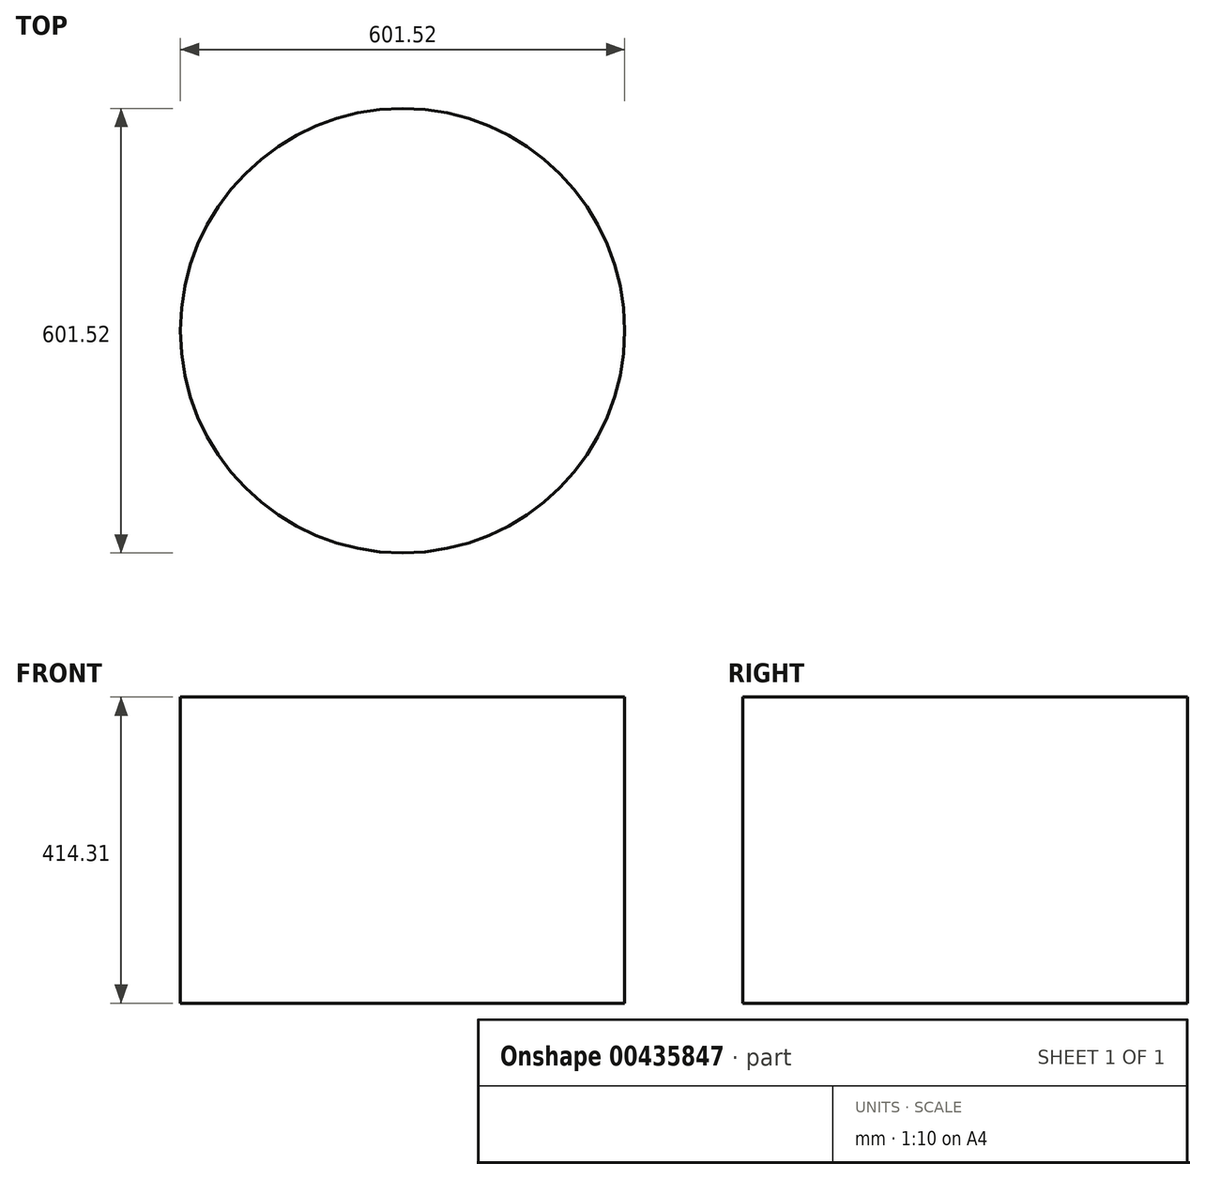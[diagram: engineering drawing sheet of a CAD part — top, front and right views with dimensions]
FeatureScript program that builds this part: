
annotation { "Feature Type Name" : "Feature", "Feature Type Description" : "" }
export const myFeature = defineFeature(function(context is Context, id is Id, definition is map)
    precondition{}
    {
        {
            var Q0;
            Q0=qCreatedBy(makeId("Top.planeOp"),FACE);
            var sketch = newSketch(context, id + "F0", { "sketchPlane" : qUnion([Q0])});
            skCircle(sketch, "E0", {"center": v(-114.9, 244.31) * mm, "radius": 300.76 * mm});
            skSolve(sketch);
        }
        {
            var Q0;
            Q0 = qSketchRegion(id + "F0", true);
            extrude(context, id + "F1", {"entities" : qUnion([Q0]), "depth" : 414.3 * mm});
        }
    });
